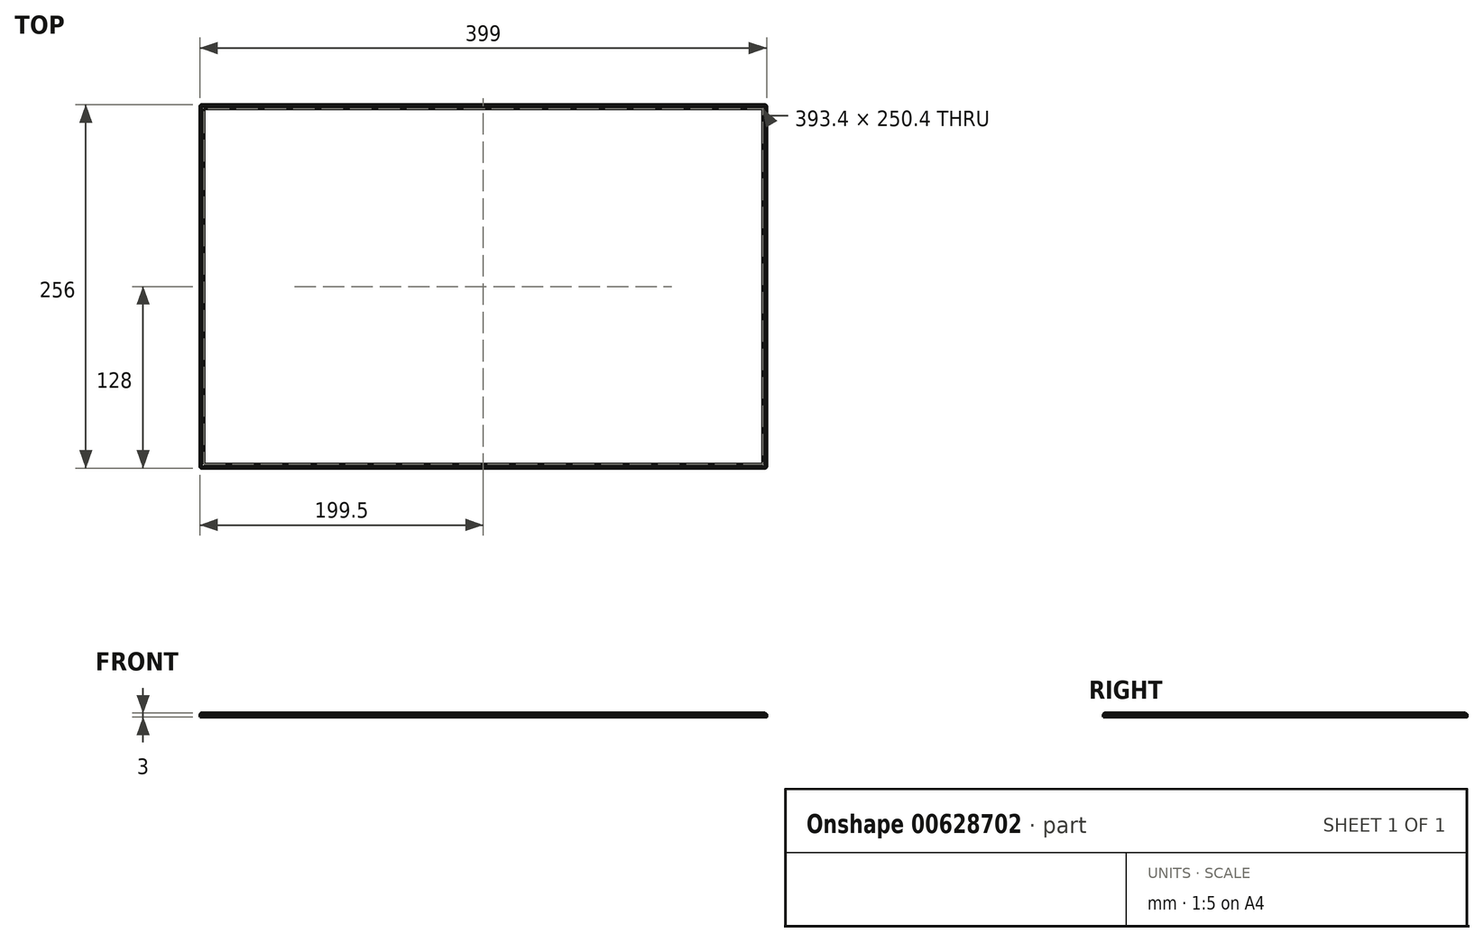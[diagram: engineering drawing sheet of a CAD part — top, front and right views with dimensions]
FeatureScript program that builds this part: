
annotation { "Feature Type Name" : "Feature", "Feature Type Description" : "" }
export const myFeature = defineFeature(function(context is Context, id is Id, definition is map)
    precondition{}
    {
        {
            var Q0;
            Q0=qCreatedBy(makeId("Top.planeOp"),FACE);
            var sketch = newSketch(context, id + "F0", { "sketchPlane" : qUnion([Q0])});
            skLineSegment(sketch, "E0.bottom", {"start": v(199.5, 128) * mm, "end": v(-199.5, 128) * mm});
            skLineSegment(sketch, "E0.top", {"start": v(199.5, -128) * mm, "end": v(-199.5, -128) * mm});
            skLineSegment(sketch, "E0.left", {"start": v(199.5, 128) * mm, "end": v(199.5, -128) * mm});
            skLineSegment(sketch, "E0.right", {"start": v(-199.5, 128) * mm, "end": v(-199.5, -128) * mm});
            skPoint(sketch, "E0.middle", {"position": v(0, 0) * mm});
            skLineSegment(sketch, "E1.0", {"start": v(-196.7, 125.2) * mm, "end": v(-196.7, -125.2) * mm});
            skLineSegment(sketch, "E1.1", {"start": v(196.7, 125.2) * mm, "end": v(-196.7, 125.2) * mm});
            skLineSegment(sketch, "E1.2", {"start": v(196.7, 125.2) * mm, "end": v(196.7, -125.2) * mm});
            skLineSegment(sketch, "E1.3", {"start": v(196.7, -125.2) * mm, "end": v(-196.7, -125.2) * mm});
            skSolve(sketch);
        }
        {
            var Q0;
            Q0 = qSketchRegion(id + "F0", true);
            extrude(context, id + "F1", {"entities" : qUnion([Q0]), "endBound" : BoundingType.SYMMETRIC, "depth" : 3 * mm, "offsetDistance" : 25 * mm});
        }
        {
            var Q0;
            Q0=makeQuery(id+"F1.opExtrude","CAP_EDGE",EDGE,{"disambiguationData":[OSD([sQuery(id+"F0.wireOp",EDGE,"E0.top")])],"isStart":false});
            var Q1;
            Q1=makeQuery(id+"F1.opExtrude","CAP_EDGE",EDGE,{"disambiguationData":[OSD([sQuery(id+"F0.wireOp",EDGE,"E0.right")])],"isStart":false});
            var Q2;
            Q2=makeQuery(id+"F1.opExtrude","CAP_EDGE",EDGE,{"disambiguationData":[OSD([sQuery(id+"F0.wireOp",EDGE,"E0.bottom")])],"isStart":false});
            var Q3;
            Q3=makeQuery(id+"F1.opExtrude","CAP_EDGE",EDGE,{"disambiguationData":[OSD([sQuery(id+"F0.wireOp",EDGE,"E0.left")])],"isStart":false});
            chamfer(context, id + "F2", {"entities" : qUnion([Q0, Q1, Q2, Q3]), "width" : 1 * mm, "tangentPropagation" : true});
        }
        {
            var Q0;
            Q0=makeQuery(id+"F1.opExtrude","SWEPT_EDGE",EDGE,{"disambiguationData":[OSD([sQuery(id+"F0.wireOp",EDGE,"E0.top"),sQuery(id+"F0.wireOp",EDGE,"E0.left")])]});
            var Q1;
            Q1=makeQuery(id+"F2.opChamfer","BLEND_EDGE",EDGE,{"blendedFrom":[makeQuery(id+"F1.opExtrude","CAP_EDGE",EDGE,{"disambiguationData":[OSD([sQuery(id+"F0.wireOp",EDGE,"E0.top")])],"isStart":false}),makeQuery(id+"F1.opExtrude","CAP_EDGE",EDGE,{"disambiguationData":[OSD([sQuery(id+"F0.wireOp",EDGE,"E0.left")])],"isStart":false})],"blendedInto":[]});
            var Q2;
            Q2=makeQuery(id+"F2.opChamfer","BLEND_EDGE",EDGE,{"blendedFrom":[makeQuery(id+"F1.opExtrude","CAP_EDGE",EDGE,{"disambiguationData":[OSD([sQuery(id+"F0.wireOp",EDGE,"E0.top")])],"isStart":false}),makeQuery(id+"F1.opExtrude","CAP_EDGE",EDGE,{"disambiguationData":[OSD([sQuery(id+"F0.wireOp",EDGE,"E0.right")])],"isStart":false})],"blendedInto":[]});
            var Q3;
            Q3=makeQuery(id+"F1.opExtrude","SWEPT_EDGE",EDGE,{"disambiguationData":[OSD([sQuery(id+"F0.wireOp",EDGE,"E0.top"),sQuery(id+"F0.wireOp",EDGE,"E0.right")])]});
            var Q4;
            Q4=makeQuery(id+"F2.opChamfer","BLEND_EDGE",EDGE,{"blendedFrom":[makeQuery(id+"F1.opExtrude","CAP_EDGE",EDGE,{"disambiguationData":[OSD([sQuery(id+"F0.wireOp",EDGE,"E0.bottom")])],"isStart":false}),makeQuery(id+"F1.opExtrude","CAP_EDGE",EDGE,{"disambiguationData":[OSD([sQuery(id+"F0.wireOp",EDGE,"E0.right")])],"isStart":false})],"blendedInto":[]});
            var Q5;
            Q5=makeQuery(id+"F1.opExtrude","SWEPT_EDGE",EDGE,{"disambiguationData":[OSD([sQuery(id+"F0.wireOp",EDGE,"E0.bottom"),sQuery(id+"F0.wireOp",EDGE,"E0.right")])]});
            var Q6;
            Q6=makeQuery(id+"F2.opChamfer","BLEND_EDGE",EDGE,{"blendedFrom":[makeQuery(id+"F1.opExtrude","CAP_EDGE",EDGE,{"disambiguationData":[OSD([sQuery(id+"F0.wireOp",EDGE,"E0.bottom")])],"isStart":false}),makeQuery(id+"F1.opExtrude","CAP_EDGE",EDGE,{"disambiguationData":[OSD([sQuery(id+"F0.wireOp",EDGE,"E0.left")])],"isStart":false})],"blendedInto":[]});
            var Q7;
            Q7=makeQuery(id+"F1.opExtrude","SWEPT_EDGE",EDGE,{"disambiguationData":[OSD([sQuery(id+"F0.wireOp",EDGE,"E0.bottom"),sQuery(id+"F0.wireOp",EDGE,"E0.left")])]});
            fillet(context, id + "F3", {"entities" : qUnion([Q0, Q1, Q2, Q3, Q4, Q5, Q6, Q7]), "radius" : 1 * mm, "tangentPropagation" : true, "allowEdgeOverflow" : false});
        }
    });
